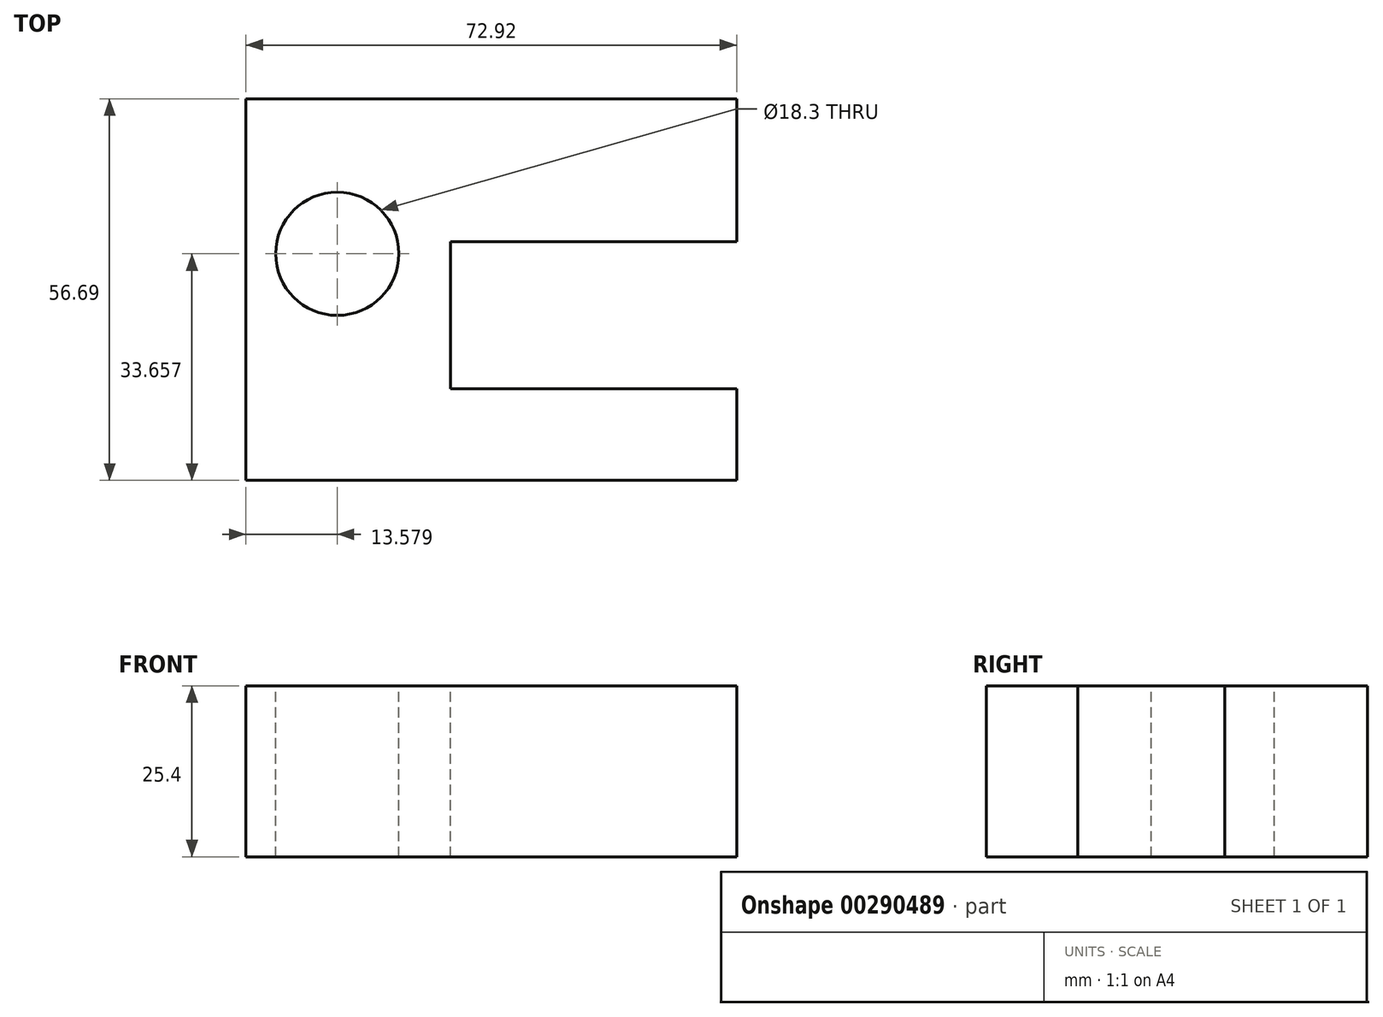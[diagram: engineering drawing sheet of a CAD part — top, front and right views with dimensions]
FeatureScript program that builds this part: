
annotation { "Feature Type Name" : "Feature", "Feature Type Description" : "" }
export const myFeature = defineFeature(function(context is Context, id is Id, definition is map)
    precondition{}
    {
        {
            var Q0;
            Q0=qCreatedBy(makeId("Top.planeOp"),FACE);
            var sketch = newSketch(context, id + "F0", { "sketchPlane" : qUnion([Q0])});
            skLineSegment(sketch, "E0.bottom", {"start": v(-51.37, 31.89) * mm, "end": v(21.55, 31.89) * mm});
            skLineSegment(sketch, "E0.top", {"start": v(-51.37, -24.8) * mm, "end": v(21.55, -24.8) * mm});
            skLineSegment(sketch, "E0.left", {"start": v(-51.37, 31.89) * mm, "end": v(-51.37, -24.8) * mm});
            skLineSegment(sketch, "E0.right", {"start": v(21.55, 31.89) * mm, "end": v(21.55, -24.8) * mm});
            skLineSegment(sketch, "E1.bottom", {"start": v(36.31, -11.22) * mm, "end": v(-20.96, -11.22) * mm});
            skLineSegment(sketch, "E1.top", {"start": v(36.31, 10.63) * mm, "end": v(-20.96, 10.63) * mm});
            skLineSegment(sketch, "E1.left", {"start": v(36.31, -11.22) * mm, "end": v(36.31, 10.63) * mm});
            skLineSegment(sketch, "E1.right", {"start": v(-20.96, -11.22) * mm, "end": v(-20.96, 10.63) * mm});
            skCircle(sketch, "E2", {"center": v(-37.8, 8.86) * mm, "radius": 9.15 * mm});
            skSolve(sketch);
        }
        {
            var Q0;
            {var subQ1=sQuery(id+"F0.wireOp",EDGE,"E0.bottom");Q0=makeQuery(id+"F0.imprint","IMPRINT",FACE,{"disambiguationData":[TD([[makeQuery(id+"F0.imprint","IMPRINT",EDGE,{"derivedFrom":subQ1}),-1.0]])]});}
            extrude(context, id + "F1", {"entities" : qUnion([Q0]), "oppositeDirection" : true, "depth" : 25.4 * mm});
        }
    });
